# Revit family: EU_OD-Double-Glass
name_source: partatom
category: Doors
revit_build: Autodesk Revit 2014 (Build: 20130308_1515(x64)
units: mm (PartAtom-declared; Revit-internal decimal feet)

## types (1)
- 18x21
    Doorleaf = EU_General Wood
    Doorleaf Dim Bottom = 200 mm  [stored 0.656168 ft]
    Doorleaf Dim Left = 100 mm  [stored 0.328084 ft]
    Doorleaf Dim Right = 100 mm  [stored 0.328084 ft]
    Doorleaf Dim Top = 100 mm  [stored 0.328084 ft]
    Doorleaf Thickness = 50 mm  [stored 0.164042 ft]
    Doornob = EU_Steel
    Frame = EU_General Wood
    Function = Interior
    Glass = EU_Glass
    Height = 2110 mm  [stored 6.92257 ft]
    Rough Height = 21 mm
    Rough Width = 18 mm
    Sash Depth = 100 mm  [stored 0.328084 ft]
    Sash Thickness = 40 mm  [stored 0.131234 ft]
    Threshold = EU_General Wood
    Type Name (in Project) = Sett inn typenr (D1)
    Wall Closure = By host
    Width = 1810 mm  [stored 5.93832 ft]

note: [stored X ft] marks values corroborated as IEEE doubles in the binary element streams (Revit-internal decimal feet)

## geometry (parser evidence)
native form markers: Sweep x1
no freeform markers — native parametric forms only
